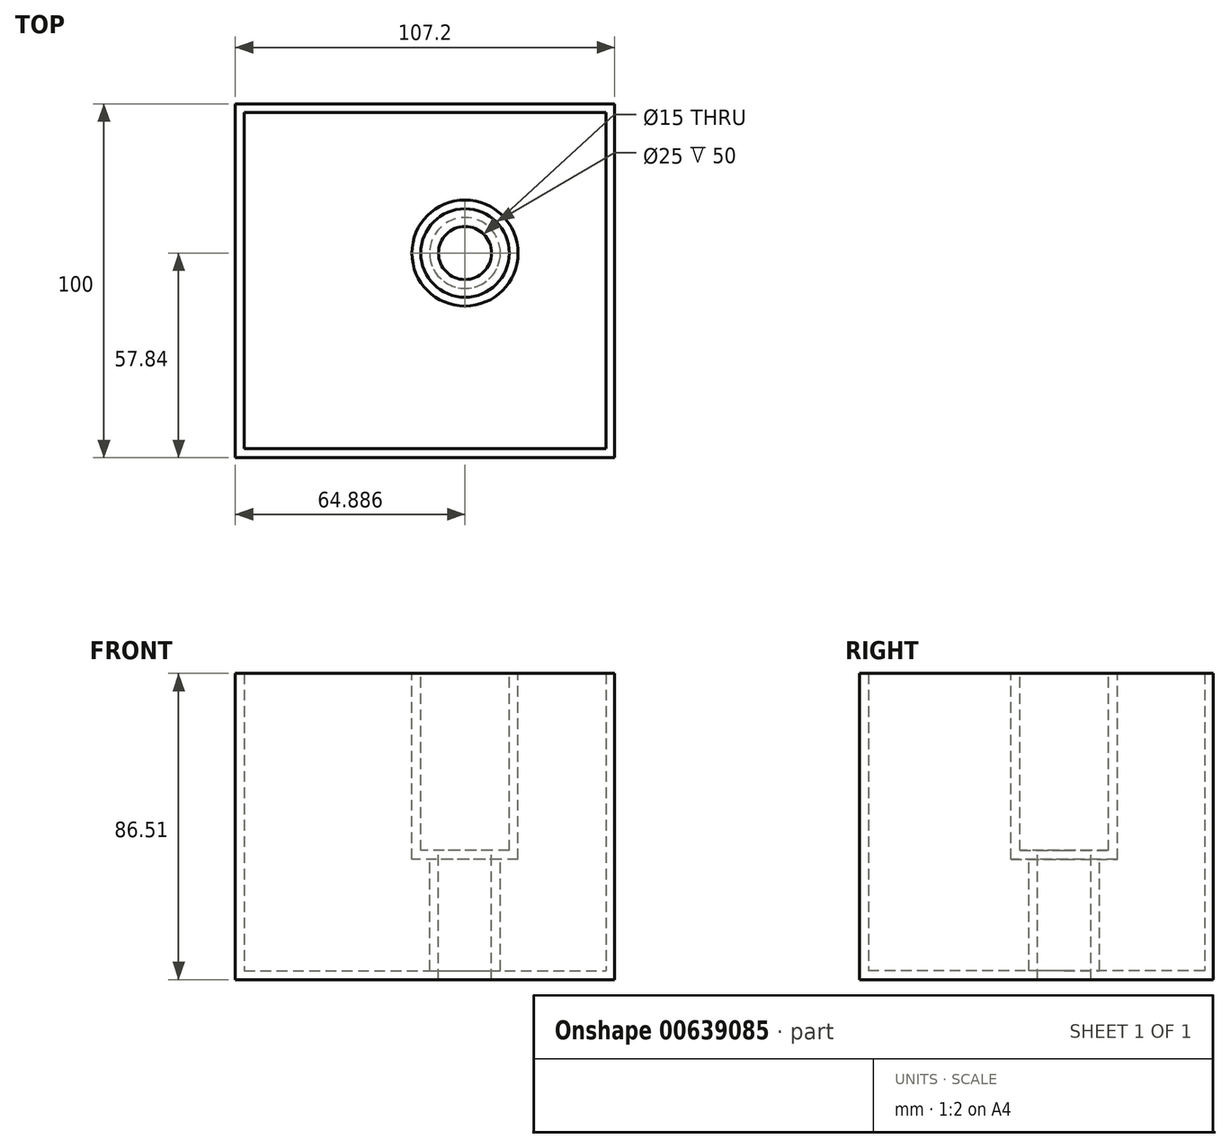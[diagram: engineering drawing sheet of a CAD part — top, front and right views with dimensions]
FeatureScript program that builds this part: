
annotation { "Feature Type Name" : "Feature", "Feature Type Description" : "" }
export const myFeature = defineFeature(function(context is Context, id is Id, definition is map)
    precondition{}
    {
        {
            var Q0;
            Q0=qCreatedBy(makeId("Front.planeOp"),FACE);
            var sketch = newSketch(context, id + "F0", { "sketchPlane" : qUnion([Q0])});
            skLineSegment(sketch, "E0.bottom", {"start": v(-55.7, 40.79) * mm, "end": v(51.5, 40.79) * mm});
            skLineSegment(sketch, "E0.top", {"start": v(-55.7, -45.72) * mm, "end": v(51.5, -45.72) * mm});
            skLineSegment(sketch, "E0.left", {"start": v(-55.7, 40.79) * mm, "end": v(-55.7, -45.72) * mm});
            skLineSegment(sketch, "E0.right", {"start": v(51.5, 40.79) * mm, "end": v(51.5, -45.72) * mm});
            skSolve(sketch);
        }
        {
            var Q0;
            Q0=makeQuery(id+"F0.imprint","IMPRINT",FACE,{"disambiguationData":[TD([[makeQuery(id+"F0.imprint","IMPRINT",EDGE,{"derivedFrom":sQuery(id+"F0.wireOp",EDGE,"E0.bottom")}),-1.0]])]});
            extrude(context, id + "F1", {"entities" : qUnion([Q0]), "oppositeDirection" : true, "depth" : 100 * mm, "offsetDistance" : 25 * mm});
        }
        {
            var Q0;
            Q0=makeQuery(id+"F1.opExtrude","SWEPT_FACE",FACE,{"disambiguationData":[OSD([sQuery(id+"F0.wireOp",EDGE,"E0.bottom")])]});
            var sketch = newSketch(context, id + "F2", { "sketchPlane" : qUnion([Q0])});
            skCircle(sketch, "E1", {"center": v(9.19, 57.84) * mm, "radius": 7.66 * mm});
            skSolve(sketch);
        }
        {
            var Q0;
            Q0=sQuery(id+"F2.wireOp",VERTEX,"E1.center");
            var Q1;
            Q1=makeQuery(id+"F1.opExtrude","SWEPT_BODY",BODY,{"disambiguationData":[OSD([sQuery(id+"F0.wireOp",EDGE,"E0.bottom"),sQuery(id+"F0.wireOp",EDGE,"E0.top"),sQuery(id+"F0.wireOp",EDGE,"E0.left"),sQuery(id+"F0.wireOp",EDGE,"E0.right")])]});
            hole(context, id + "F3", {"style" : HoleStyle.C_BORE, "endStyle" : HoleEndStyle.THROUGH, "holeDiameter" : 15 * mm, "cBoreDiameter" : 25 * mm, "cBoreDepth" : 50 * mm, "majorDiameter" : 5 * mm, "isTappedThrough" : true, "tappedDepth" : 12 * mm, "tapClearance" : 3, "locations" : qUnion([Q0]), "scope" : qUnion([Q1])});
        }
        {
            var Q0;
            Q0=makeQuery(id+"F1.opExtrude","SWEPT_FACE",FACE,{"disambiguationData":[OSD([sQuery(id+"F0.wireOp",EDGE,"E0.bottom")])]});
            shell(context, id + "F4", {"entities" : qUnion([Q0]), "thickness" : 2.5 * mm});
        }
    });
